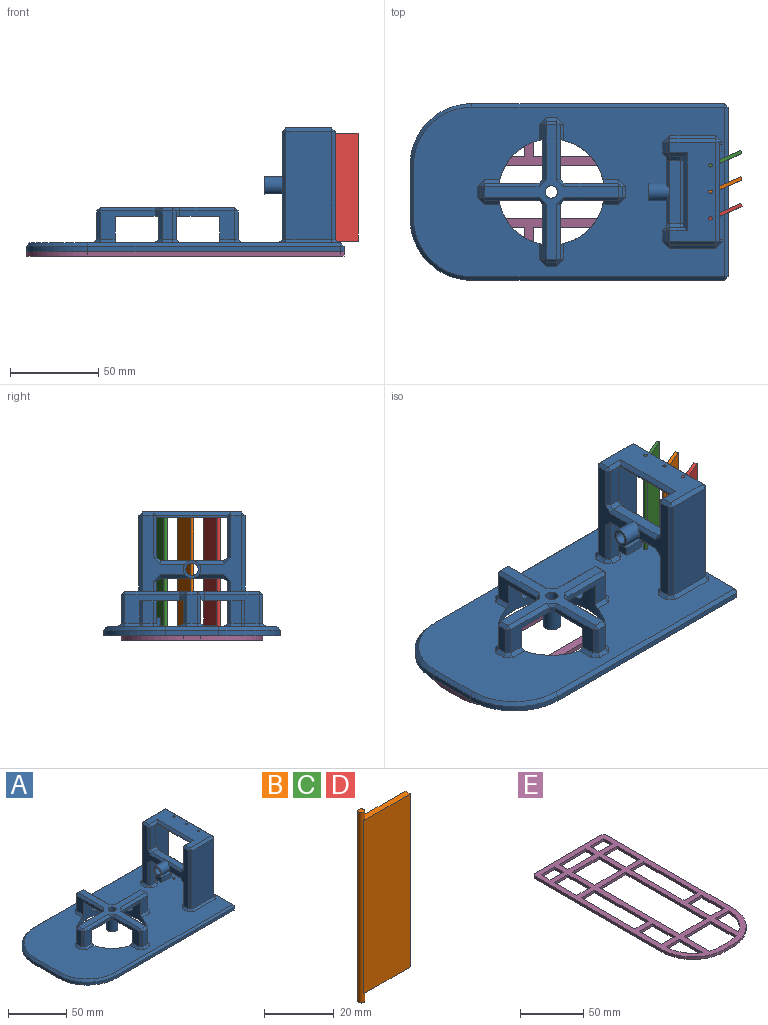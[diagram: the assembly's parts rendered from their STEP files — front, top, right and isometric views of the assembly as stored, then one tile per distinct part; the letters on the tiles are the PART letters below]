
ASSEMBLY  parts=5 mates=4
PART A: 192 faces, bbox 180x100x70 mm
  f0: plane 5x3mm, normal (-1,0,0), area 15mm2, adj f1,f2,f3,f189
  f1: plane 176x96mm, normal (0,0,1), area 12301.4mm2, adj f0,f3,f19,f26,f27,f28,f29,f48
  f2: plane 180x100mm, normal (0,0,-1), area 14548.4mm2, adj f0,f3,f20,f21,f22,f23,f24,f25
  f3: plane 67x22mm, normal (0,-1,0), area 1295mm2, adj f0,f1,f2,f4,f32,f34,f152,f181
  f4: plane 60x25.2mm, normal (1,0,0), area 430mm2, adj f3,f34,f117,f124,f125,f129,f175,f177
  f5: plane 61x24mm, normal (-1,0,0), area 485.9mm2, adj f118,f123,f126,f127,f130,f139,f148,f156
  f6: plane 61x24mm, normal (-1,0,0), area 485.9mm2, adj f118,f138,f143,f147,f155,f165,f166,f170
  f7: plane 60x25.2mm, normal (1,0,0), area 430mm2, adj f19,f34,f117,f120,f121,f125,f158,f168
  f8: plane 23.5x8mm, normal (0,-1,0), area 143mm2, adj f10,f34,f124,f137,f146,f147
  f9: plane 23.5x8mm, normal (0,1,0), area 143mm2, adj f10,f34,f120,f122,f123,f136
  f10: plane 40x1mm, normal (-1,0,0), area 40mm2, adj f8,f9,f34,f142
  f11: plane 76x76mm, normal (0,0,1), area 869.5mm2, adj f44,f64,f67,f72,f73,f76,f77,f84
  f12: plane 31x16mm, normal (0,-1,0), area 202.5mm2, adj f26,f45,f81,f91,f97,f98
  f13: plane 31x16mm, normal (0,1,0), area 202.5mm2, adj f26,f45,f70,f71,f83,f84
  f14: plane 10x10mm, normal (0,0,-1), area 40.1mm2, adj f44,f46
  f15: plane 31x16mm, normal (1,0,0), area 202.5mm2, adj f26,f45,f57,f62,f67,f68
  f16: plane 31x16mm, normal (-1,0,0), area 202.5mm2, adj f26,f45,f97,f102,f108,f109
  f17: plane 31x16mm, normal (1,0,0), area 202.5mm2, adj f26,f45,f96,f101,f106,f107
  f18: plane 31x16mm, normal (-1,0,0), area 202.5mm2, adj f26,f45,f58,f63,f71,f72
  f19: plane 62x22mm, normal (0,1,0), area 1240mm2, adj f1,f7,f32,f34,f132,f158
  f20: plane 30x3mm, normal (-1,0,0), area 90mm2, adj f2,f21,f25,f56
  f21: cylinder r=35mm len=35mm, axis (0,0,-1), area 164.9mm2, adj f2,f20,f22,f55
  f22: plane 143x3mm, normal (0,-1,0), area 429mm2, adj f2,f21,f49,f53
  f23: plane 96x3mm, normal (1,0,0), area 288mm2, adj f2,f47,f48,f49
  f24: plane 143x3mm, normal (0,1,0), area 429mm2, adj f2,f25,f47,f52
  f25: cylinder r=35mm len=35mm, axis (0,0,-1), area 164.9mm2, adj f2,f20,f24,f54
  f26: cylinder r=30mm len=60mm, axis (0,0,-1), area 1561.6mm2, adj f1,f2,f12,f13,f15,f16,f17,f18
  f27: cylinder r=1mm len=5mm, axis (0,0,-1), area 31.4mm2, adj f1,f2
  f28: cylinder r=1mm len=5mm, axis (0,0,-1), area 31.4mm2, adj f1,f2
  f29: cylinder r=1mm len=5mm, axis (0,0,-1), area 31.4mm2, adj f1,f2
  f30: plane 56x26mm, normal (0,0,1), area 1006.6mm2, adj f35,f36,f37,f127,f135,f136,f142,f145
  f31: plane 61x26mm, normal (0,1,0), area 1586mm2, adj f153,f154,f164,f165
  f32: plane 61x56mm, normal (1,0,0), area 176mm2, adj f3,f19,f34,f132,f134,f145,f152,f153
  f33: plane 61x26mm, normal (0,-1,0), area 1586mm2, adj f134,f135,f139,f140
  f34: plane 54x22mm, normal (0,0,-1), area 1074.6mm2, adj f3,f4,f7,f8,f9,f10,f19,f32
  f35: cylinder r=1mm len=3mm, axis (0,0,-1), area 18.8mm2, adj f30,f34
  f36: cylinder r=1mm len=3mm, axis (0,0,-1), area 18.8mm2, adj f30,f34
  f37: cylinder r=1mm len=3mm, axis (0,0,-1), area 18.8mm2, adj f30,f34
  f38: plane 31x16mm, normal (0,-1,0), area 202.5mm2, adj f26,f45,f80,f90,f95,f96
  f39: plane 31x16mm, normal (0,1,0), area 202.5mm2, adj f26,f45,f68,f69,f77,f78
  f40: plane 16x6mm, normal (-1,0,0), area 96mm2, adj f82,f83,f91,f92
  f41: plane 16x6mm, normal (0,-1,0), area 96mm2, adj f103,f106,f109,f112
  f42: plane 16x6mm, normal (1,0,0), area 96mm2, adj f78,f79,f89,f90
  f43: plane 16x6mm, normal (0,1,0), area 96mm2, adj f59,f62,f63,f64
  f44: cylinder r=3.5mm len=20mm, axis (0,0,-1), area 439.8mm2, adj f11,f14
  f45: plane 60x60mm, normal (0,0,-1), area 1023.9mm2, adj f12,f13,f15,f16,f17,f18,f26,f38
  f46: cylinder r=5mm len=15mm, axis (0,0,1), area 471.2mm2, adj f14,f45
  f47: plane 3x2mm, normal (0.71,0.71,0), area 8.5mm2, adj f2,f23,f24,f50
  f48: plane 96x2mm, normal (0.71,0,0.71), area 271.5mm2, adj f1,f23,f50,f51
  f49: plane 3x2mm, normal (0.71,-0.71,0), area 8.5mm2, adj f2,f22,f23,f51
  f50: plane 2x2mm, normal (0.58,0.58,0.58), area 3.5mm2, adj f47,f48,f52
  f51: plane 2x2mm, normal (0.58,-0.58,0.58), area 3.5mm2, adj f48,f49,f53
  f52: plane 143x2mm, normal (0,0.71,0.71), area 404.5mm2, adj f1,f24,f50,f54
  f53: plane 143x2mm, normal (0,-0.71,0.71), area 404.5mm2, adj f1,f22,f51,f55
  f54: cone r=33mm half-angle=45deg, axis (0,0,-1), area 151.1mm2, adj f1,f25,f52,f56
  f55: cone r=33mm half-angle=45deg, axis (0,0,-1), area 151.1mm2, adj f1,f21,f53,f56
  f56: plane 30x2mm, normal (-0.71,0,0.71), area 84.9mm2, adj f1,f20,f54,f55
  f57: plane 8.84x2.01mm, normal (0.71,0,0.71), area 24.4mm2, adj f1,f15,f26,f60
  f58: plane 8.84x2.01mm, normal (-0.71,0,0.71), area 24.4mm2, adj f1,f18,f26,f61
  f59: plane 6x2mm, normal (0,0.71,0.71), area 17mm2, adj f1,f43,f60,f61
  f60: plane 4x4mm, normal (0.58,0.58,0.58), area 10.4mm2, adj f1,f57,f59,f62
  f61: plane 4x4mm, normal (-0.58,0.58,0.58), area 10.4mm2, adj f1,f58,f59,f63
  f62: plane 16x2mm, normal (0.71,0.71,0), area 45.3mm2, adj f15,f43,f60,f65
  f63: plane 16x2mm, normal (-0.71,0.71,0), area 45.3mm2, adj f18,f43,f61,f66
  f64: plane 6x2mm, normal (0,0.71,0.71), area 17mm2, adj f11,f43,f65,f66
  f65: plane 2x2mm, normal (0.58,0.58,0.58), area 3.5mm2, adj f62,f64,f67
  f66: plane 2x2mm, normal (-0.58,0.58,0.58), area 3.5mm2, adj f63,f64,f72
  f67: plane 31x2mm, normal (0.71,0,0.71), area 87.7mm2, adj f11,f15,f65,f73
  f68: plane 3x2mm, normal (0.71,0.71,0), area 8.5mm2, adj f15,f39,f45,f73
  f69: plane 8.84x2.01mm, normal (0,0.71,0.71), area 24.4mm2, adj f1,f26,f39,f74
  f70: plane 8.84x2.01mm, normal (0,0.71,0.71), area 24.4mm2, adj f1,f13,f26,f75
  f71: plane 3x2mm, normal (-0.71,0.71,0), area 8.5mm2, adj f13,f18,f45,f76
  f72: plane 31x2mm, normal (-0.71,0,0.71), area 87.7mm2, adj f11,f18,f66,f76
  f73: plane 4x4mm, normal (0.58,0.58,0.58), area 10.4mm2, adj f11,f67,f68,f77
  f74: plane 4x4mm, normal (0.58,0.58,0.58), area 10.4mm2, adj f1,f69,f78,f79
  f75: plane 4x4mm, normal (-0.58,0.58,0.58), area 10.4mm2, adj f1,f70,f82,f83
  f76: plane 4x4mm, normal (-0.58,0.58,0.58), area 10.4mm2, adj f11,f71,f72,f84
  f77: plane 31x2mm, normal (0,0.71,0.71), area 87.7mm2, adj f11,f39,f73,f85
  f78: plane 16x2mm, normal (0.71,0.71,0), area 45.3mm2, adj f39,f42,f74,f85
  f79: plane 6x2mm, normal (0.71,0,0.71), area 17mm2, adj f1,f42,f74,f86
  f80: plane 8.84x2.01mm, normal (0,-0.71,0.71), area 24.4mm2, adj f1,f26,f38,f86
  f81: plane 8.84x2.01mm, normal (0,-0.71,0.71), area 24.4mm2, adj f1,f12,f26,f87
  f82: plane 6x2mm, normal (-0.71,0,0.71), area 17mm2, adj f1,f40,f75,f87
  f83: plane 16x2mm, normal (-0.71,0.71,0), area 45.3mm2, adj f13,f40,f75,f88
  f84: plane 31x2mm, normal (0,0.71,0.71), area 87.7mm2, adj f11,f13,f76,f88
  f85: plane 2x2mm, normal (0.58,0.58,0.58), area 3.5mm2, adj f77,f78,f89
  f86: plane 4x4mm, normal (0.58,-0.58,0.58), area 10.4mm2, adj f1,f79,f80,f90
  f87: plane 4x4mm, normal (-0.58,-0.58,0.58), area 10.4mm2, adj f1,f81,f82,f91
  f88: plane 2x2mm, normal (-0.58,0.58,0.58), area 3.5mm2, adj f83,f84,f92
  f89: plane 6x2mm, normal (0.71,0,0.71), area 17mm2, adj f11,f42,f85,f93
  f90: plane 16x2mm, normal (0.71,-0.71,0), area 45.3mm2, adj f38,f42,f86,f93
  f91: plane 16x2mm, normal (-0.71,-0.71,0), area 45.3mm2, adj f12,f40,f87,f94
  f92: plane 6x2mm, normal (-0.71,0,0.71), area 17mm2, adj f11,f40,f88,f94
  f93: plane 2x2mm, normal (0.58,-0.58,0.58), area 3.5mm2, adj f89,f90,f95
  f94: plane 2x2mm, normal (-0.58,-0.58,0.58), area 3.5mm2, adj f91,f92,f98
  f95: plane 31x2mm, normal (0,-0.71,0.71), area 87.7mm2, adj f11,f38,f93,f99
  f96: plane 3x2mm, normal (0.71,-0.71,0), area 8.5mm2, adj f17,f38,f45,f99
  f97: plane 3x2mm, normal (-0.71,-0.71,0), area 8.5mm2, adj f12,f16,f45,f100
  f98: plane 31x2mm, normal (0,-0.71,0.71), area 87.7mm2, adj f11,f12,f94,f100
  f99: plane 4x4mm, normal (0.58,-0.58,0.58), area 10.4mm2, adj f11,f95,f96,f101
  f100: plane 4x4mm, normal (-0.58,-0.58,0.58), area 10.4mm2, adj f11,f97,f98,f102
  f101: plane 31x2mm, normal (0.71,0,0.71), area 87.7mm2, adj f11,f17,f99,f104
  f102: plane 31x2mm, normal (-0.71,0,0.71), area 87.7mm2, adj f11,f16,f100,f105
  f103: plane 6x2mm, normal (0,-0.71,0.71), area 17mm2, adj f11,f41,f104,f105
  f104: plane 2x2mm, normal (0.58,-0.58,0.58), area 3.5mm2, adj f101,f103,f106
  f105: plane 2x2mm, normal (-0.58,-0.58,0.58), area 3.5mm2, adj f102,f103,f109
  f106: plane 16x2mm, normal (0.71,-0.71,0), area 45.3mm2, adj f17,f41,f104,f110
  f107: plane 8.84x2.01mm, normal (0.71,0,0.71), area 24.4mm2, adj f1,f17,f26,f110
  f108: plane 8.84x2.01mm, normal (-0.71,0,0.71), area 24.4mm2, adj f1,f16,f26,f111
  f109: plane 16x2mm, normal (-0.71,-0.71,0), area 45.3mm2, adj f16,f41,f105,f111
  f110: plane 4x4mm, normal (0.58,-0.58,0.58), area 10.4mm2, adj f1,f106,f107,f112
  f111: plane 4x4mm, normal (-0.58,-0.58,0.58), area 10.4mm2, adj f1,f108,f109,f112
  f112: plane 6x2mm, normal (0,-0.71,0.71), area 17mm2, adj f1,f41,f110,f111
  f113: plane 23.5x6mm, normal (0,-1,0), area 141mm2, adj f173,f174,f178,f179
  f114: plane 23.5x6mm, normal (0,1,0), area 141mm2, adj f156,f157,f167,f168
  f115: plane 36x6mm, normal (0,0,-1), area 216mm2, adj f161,f166,f167,f174,f175
  f116: plane 36x6mm, normal (0,0,1), area 216mm2, adj f122,f125,f130,f137,f138
  f117: cylinder r=3.5mm len=20mm, axis (1,0,0), area 437.3mm2, adj f4,f7,f119,f125,f175
  f118: cylinder r=5mm len=12mm, axis (1,0,0), area 338.5mm2, adj f5,f6,f119,f130,f138,f161,f166
  f119: plane 10x10mm, normal (-1,0,0), area 40.1mm2, adj f117,f118
  f120: plane 22.5x2mm, normal (0.71,0.71,0), area 63.6mm2, adj f7,f9,f34,f121
  f121: plane 4x4mm, normal (0.58,0.58,0.58), area 10.4mm2, adj f7,f120,f122,f125
  f122: plane 6x2mm, normal (0,0.71,0.71), area 17mm2, adj f9,f116,f121,f126
  f123: plane 23.5x2mm, normal (-0.71,0.71,0), area 66.5mm2, adj f5,f9,f126,f128
  f124: plane 22.5x2mm, normal (0.71,-0.71,0), area 63.6mm2, adj f4,f8,f34,f129
  f125: plane 36x2mm, normal (0.71,0,0.71), area 100.1mm2, adj f4,f7,f116,f117,f121,f129
  f126: plane 4x4mm, normal (-0.58,0.58,0.58), area 10.4mm2, adj f5,f122,f123,f130
  f127: plane 6x2mm, normal (-0.71,0,0.71), area 17mm2, adj f5,f30,f128,f131
  f128: plane 2x2mm, normal (-0.58,0.58,0.58), area 3.5mm2, adj f123,f127,f136
  f129: plane 4x4mm, normal (0.58,-0.58,0.58), area 10.4mm2, adj f4,f124,f125,f137
  f130: plane 18x2mm, normal (-0.71,0,0.71), area 43mm2, adj f5,f116,f118,f126
  f131: plane 2x2mm, normal (-0.58,-0.58,0.58), area 3.5mm2, adj f127,f135,f139
  f132: plane 2x2mm, normal (0.71,0,0.71), area 2.8mm2, adj f1,f19,f32,f133
  f133: plane 4x4mm, normal (0.58,-0.58,0.58), area 10.4mm2, adj f1,f132,f134,f140
  f134: plane 61x2mm, normal (0.71,-0.71,0), area 172.5mm2, adj f32,f33,f133,f141
  f135: plane 26x2mm, normal (0,-0.71,0.71), area 73.5mm2, adj f30,f33,f131,f141
  f136: plane 10x2mm, normal (0,0.71,0.71), area 25.5mm2, adj f9,f30,f128,f142
  f137: plane 6x2mm, normal (0,-0.71,0.71), area 17mm2, adj f8,f116,f129,f143
  f138: plane 18x2mm, normal (-0.71,0,0.71), area 43mm2, adj f6,f116,f118,f143
  f139: plane 61x2mm, normal (-0.71,-0.71,0), area 172.5mm2, adj f5,f33,f131,f144
  f140: plane 26x2mm, normal (0,-0.71,0.71), area 73.5mm2, adj f1,f33,f133,f144
  f141: plane 2x2mm, normal (0.58,-0.58,0.58), area 3.5mm2, adj f134,f135,f145
  f142: plane 44x2mm, normal (-0.71,0,0.71), area 118.8mm2, adj f10,f30,f136,f146
  f143: plane 4x4mm, normal (-0.58,-0.58,0.58), area 10.4mm2, adj f6,f137,f138,f147
  f144: plane 4x4mm, normal (-0.58,-0.58,0.58), area 10.4mm2, adj f1,f139,f140,f148
  f145: plane 56x2mm, normal (0.71,0,0.71), area 158.4mm2, adj f30,f32,f141,f149
  f146: plane 10x2mm, normal (0,-0.71,0.71), area 25.5mm2, adj f8,f30,f142,f150
  f147: plane 23.5x2mm, normal (-0.71,-0.71,0), area 66.5mm2, adj f6,f8,f143,f150
  f148: plane 6x2mm, normal (-0.71,0,0.71), area 17mm2, adj f1,f5,f144,f151
  f149: plane 2x2mm, normal (0.58,0.58,0.58), area 3.5mm2, adj f145,f153,f154
  f150: plane 2x2mm, normal (-0.58,-0.58,0.58), area 3.5mm2, adj f146,f147,f155
  f151: plane 4x4mm, normal (-0.58,0.58,0.58), area 10.4mm2, adj f1,f148,f156,f157
  f152: plane 2x2mm, normal (0.71,0,0.71), area 2.8mm2, adj f1,f3,f32,f159
  f153: plane 61x2mm, normal (0.71,0.71,0), area 172.5mm2, adj f31,f32,f149,f159
  f154: plane 26x2mm, normal (0,0.71,0.71), area 73.5mm2, adj f30,f31,f149,f160
  f155: plane 6x2mm, normal (-0.71,0,0.71), area 17mm2, adj f6,f30,f150,f160
  f156: plane 23.5x2mm, normal (-0.71,0.71,0), area 66.5mm2, adj f5,f114,f151,f162
  f157: plane 6x2mm, normal (0,0.71,0.71), area 17mm2, adj f1,f114,f151,f163
  f158: plane 5x2mm, normal (0.71,0,0.71), area 14.1mm2, adj f1,f7,f19,f163
  f159: plane 4x4mm, normal (0.58,0.58,0.58), area 10.4mm2, adj f1,f152,f153,f164
  f160: plane 2x2mm, normal (-0.58,0.58,0.58), area 3.5mm2, adj f154,f155,f165
  f161: plane 18x2mm, normal (-0.71,0,-0.71), area 43mm2, adj f5,f115,f118,f162
  f162: plane 4x4mm, normal (-0.58,0.58,-0.58), area 10.4mm2, adj f5,f156,f161,f167
  f163: plane 4x4mm, normal (0.58,0.58,0.58), area 10.4mm2, adj f1,f157,f158,f168
  f164: plane 26x2mm, normal (0,0.71,0.71), area 73.5mm2, adj f1,f31,f159,f169
  f165: plane 61x2mm, normal (-0.71,0.71,0), area 172.5mm2, adj f6,f31,f160,f169
  f166: plane 18x2mm, normal (-0.71,0,-0.71), area 43mm2, adj f6,f115,f118,f170
  f167: plane 6x2mm, normal (0,0.71,-0.71), area 17mm2, adj f114,f115,f162,f171
  f168: plane 23.5x2mm, normal (0.71,0.71,0), area 66.5mm2, adj f7,f114,f163,f171
  f169: plane 4x4mm, normal (-0.58,0.58,0.58), area 10.4mm2, adj f1,f164,f165,f172
  f170: plane 4x4mm, normal (-0.58,-0.58,-0.58), area 10.4mm2, adj f6,f166,f173,f174
  f171: plane 4x4mm, normal (0.58,0.58,-0.58), area 10.4mm2, adj f7,f167,f168,f175
  f172: plane 6x2mm, normal (-0.71,0,0.71), area 17mm2, adj f1,f6,f169,f176
  f173: plane 23.5x2mm, normal (-0.71,-0.71,0), area 66.5mm2, adj f6,f113,f170,f176
  f174: plane 6x2mm, normal (0,-0.71,-0.71), area 17mm2, adj f113,f115,f170,f177
  f175: plane 36x2mm, normal (0.71,0,-0.71), area 100.1mm2, adj f4,f7,f115,f117,f171,f177
  f176: plane 4x4mm, normal (-0.58,-0.58,0.58), area 10.4mm2, adj f1,f172,f173,f178
  f177: plane 4x4mm, normal (0.58,-0.58,-0.58), area 10.4mm2, adj f4,f174,f175,f179
  f178: plane 6x2mm, normal (0,-0.71,0.71), area 17mm2, adj f1,f113,f176,f180
  f179: plane 23.5x2mm, normal (0.71,-0.71,0), area 66.5mm2, adj f4,f113,f177,f180
  f180: plane 4x4mm, normal (0.58,-0.58,0.58), area 10.4mm2, adj f1,f178,f179,f181
  f181: plane 5x2mm, normal (0.71,0,0.71), area 14.1mm2, adj f1,f3,f4,f180
  f182: plane 10x6mm, normal (1,0,0), area 60mm2, adj f2,f3,f186,f187
  f183: plane 9x5mm, normal (-1,0,0), area 45mm2, adj f1,f3,f184,f187
  f184: plane 12x5mm, normal (0,-1,0), area 60mm2, adj f1,f183,f185,f187
  f185: plane 5x3mm, normal (1,0,0), area 15mm2, adj f1,f184,f186,f187
  f186: plane 14x10mm, normal (0,1,0), area 115mm2, adj f1,f2,f182,f185,f187,f188
  f187: plane 12x9mm, normal (0,0,1), area 54mm2, adj f3,f182,f183,f184,f185,f186
  f188: plane 5x2mm, normal (-1,0,0), area 10mm2, adj f1,f2,f186,f190
  f189: plane 5x1mm, normal (0,-1,0), area 5mm2, adj f0,f1,f2,f191
  f190: plane 5x1mm, normal (0,1,0), area 5mm2, adj f1,f2,f188,f191
  f191: plane 5x1mm, normal (-1,0,0), area 5mm2, adj f1,f2,f189,f190
PART B: 8 faces, bbox 20x2x67 mm
  f0: plane 2x2mm, normal (0,0,-1), area 3.1mm2, adj f7
  f1: plane 19x2mm, normal (0,0,-1), area 36.4mm2, adj f2,f5,f6,f7
  f2: plane 61x2mm, normal (1,0,0), area 122mm2, adj f1,f3,f5,f6
  f3: plane 19x2mm, normal (0,0,1), area 36.4mm2, adj f2,f5,f6,f7
  f4: plane 2x2mm, normal (0,0,1), area 3.1mm2, adj f7
  f5: plane 61x19mm, normal (0,-1,0), area 1159mm2, adj f1,f2,f3,f7
  f6: plane 61x19mm, normal (0,1,0), area 1159mm2, adj f1,f2,f3,f7
  f7: cylinder r=1mm len=67mm, axis (0,0,-1), area 229.3mm2, adj f0,f1,f3,f4,f5,f6
PART C: same geometry as B
PART D: same geometry as B
PART E: 66 faces, bbox 80x180x2.5 mm
  f0: plane 15x2.5mm, normal (0,1,0), area 37.5mm2, adj f1,f61,f62,f63
  f1: plane 25x2.5mm, normal (1,0,0), area 62.5mm2, adj f0,f2,f62,f63
  f2: plane 15x2.5mm, normal (0,-1,0), area 37.5mm2, adj f1,f61,f62,f63
  f3: plane 15x2.5mm, normal (0,1,0), area 37.5mm2, adj f4,f47,f62,f63
  f4: plane 60x2.5mm, normal (1,0,0), area 150mm2, adj f3,f5,f62,f63
  f5: plane 15x2.5mm, normal (0,-1,0), area 37.5mm2, adj f4,f47,f62,f63
  f6: plane 15x2.5mm, normal (0,1,0), area 37.5mm2, adj f7,f48,f62,f63
  f7: plane 25x2.5mm, normal (1,0,0), area 62.5mm2, adj f6,f8,f62,f63
  f8: plane 15x2.5mm, normal (0,-1,0), area 37.5mm2, adj f7,f48,f62,f63
  f9: plane 25.98x2.5mm, normal (-1,0,0), area 65mm2, adj f10,f49,f62,f63
  f10: cylinder r=30mm len=25.98mm, axis (0,0,-1), area 78.5mm2, adj f9,f49,f62,f63
  f11: plane 28.28x2.5mm, normal (-1,0,0), area 70.7mm2, adj f12,f50,f62,f63
  f12: cylinder r=30mm len=10mm, axis (0,0,-1), area 25.5mm2, adj f11,f13,f62,f63
  f13: plane 10x2.5mm, normal (0,1,0), area 25mm2, adj f12,f14,f62,f63
  f14: cylinder r=30mm len=10mm, axis (0,0,-1), area 25.5mm2, adj f13,f15,f62,f63
  f15: plane 28.28x2.5mm, normal (1,0,0), area 70.7mm2, adj f14,f50,f62,f63
  f16: plane 15x2.5mm, normal (0,-1,0), area 37.5mm2, adj f17,f51,f62,f63
  f17: cylinder r=30mm len=25.98mm, axis (0,0,-1), area 78.5mm2, adj f16,f51,f62,f63
  f18: plane 15x2.5mm, normal (0,-1,0), area 37.5mm2, adj f19,f52,f62,f63
  f19: plane 25x2.5mm, normal (-1,0,0), area 62.5mm2, adj f18,f20,f62,f63
  f20: plane 15x2.5mm, normal (0,1,0), area 37.5mm2, adj f19,f52,f62,f63
  f21: plane 15x2.5mm, normal (0,-1,0), area 37.5mm2, adj f22,f53,f62,f63
  f22: plane 60x2.5mm, normal (-1,0,0), area 150mm2, adj f21,f23,f62,f63
  f23: plane 15x2.5mm, normal (0,1,0), area 37.5mm2, adj f22,f53,f62,f63
  f24: plane 15x2.5mm, normal (0,-1,0), area 37.5mm2, adj f25,f54,f62,f63
  f25: plane 25x2.5mm, normal (-1,0,0), area 62.5mm2, adj f24,f26,f62,f63
  f26: plane 15x2.5mm, normal (0,1,0), area 37.5mm2, adj f25,f54,f62,f63
  f27: plane 10x2.5mm, normal (1,0,0), area 25mm2, adj f28,f55,f62,f63
  f28: plane 15x2.5mm, normal (0,-1,0), area 37.5mm2, adj f27,f29,f62,f63
  f29: plane 10x2.5mm, normal (-1,0,0), area 25mm2, adj f28,f55,f62,f63
  f30: plane 10x2.5mm, normal (1,0,0), area 25mm2, adj f31,f56,f62,f63
  f31: plane 30x2.5mm, normal (0,-1,0), area 75mm2, adj f30,f32,f62,f63
  f32: plane 10x2.5mm, normal (-1,0,0), area 25mm2, adj f31,f56,f62,f63
  f33: plane 76x2.5mm, normal (0,1,0), area 190mm2, adj f62,f63,f64,f65
  f34: plane 143x2.5mm, normal (-1,0,0), area 357.5mm2, adj f35,f62,f63,f64
  f35: cylinder r=35mm len=35mm, axis (0,0,-1), area 137.4mm2, adj f34,f36,f62,f63
  f36: plane 10x2.5mm, normal (0,-1,0), area 25mm2, adj f35,f37,f62,f63
  f37: cylinder r=35mm len=35mm, axis (0,0,-1), area 137.4mm2, adj f36,f57,f62,f63
  f38: plane 10x2.5mm, normal (1,0,0), area 25mm2, adj f39,f58,f62,f63
  f39: plane 15x2.5mm, normal (0,-1,0), area 37.5mm2, adj f38,f40,f62,f63
  f40: plane 10x2.5mm, normal (-1,0,0), area 25mm2, adj f39,f58,f62,f63
  f41: plane 30x2.5mm, normal (0,1,0), area 75mm2, adj f42,f59,f62,f63
  f42: plane 25x2.5mm, normal (1,0,0), area 62.5mm2, adj f41,f43,f62,f63
  f43: plane 30x2.5mm, normal (0,-1,0), area 75mm2, adj f42,f59,f62,f63
  f44: plane 90x2.5mm, normal (1,0,0), area 225mm2, adj f45,f60,f62,f63
  f45: plane 30x2.5mm, normal (0,-1,0), area 75mm2, adj f44,f46,f62,f63
  f46: plane 90x2.5mm, normal (-1,0,0), area 225mm2, adj f45,f60,f62,f63
  f47: plane 60x2.5mm, normal (-1,0,0), area 150mm2, adj f3,f5,f62,f63
  f48: plane 25x2.5mm, normal (-1,0,0), area 62.5mm2, adj f6,f8,f62,f63
  f49: plane 15x2.5mm, normal (0,-1,0), area 37.5mm2, adj f9,f10,f62,f63
  f50: plane 30x2.5mm, normal (0,-1,0), area 75mm2, adj f11,f15,f62,f63
  f51: plane 25.98x2.5mm, normal (1,0,0), area 65mm2, adj f16,f17,f62,f63
  f52: plane 25x2.5mm, normal (1,0,0), area 62.5mm2, adj f18,f20,f62,f63
  f53: plane 60x2.5mm, normal (1,0,0), area 150mm2, adj f21,f23,f62,f63
  f54: plane 25x2.5mm, normal (1,0,0), area 62.5mm2, adj f24,f26,f62,f63
  f55: plane 15x2.5mm, normal (0,1,0), area 37.5mm2, adj f27,f29,f62,f63
  f56: plane 30x2.5mm, normal (0,1,0), area 75mm2, adj f30,f32,f62,f63
  f57: plane 143x2.5mm, normal (1,0,0), area 357.5mm2, adj f37,f62,f63,f65
  f58: plane 15x2.5mm, normal (0,1,0), area 37.5mm2, adj f38,f40,f62,f63
  f59: plane 25x2.5mm, normal (-1,0,0), area 62.5mm2, adj f41,f43,f62,f63
  f60: plane 30x2.5mm, normal (0,1,0), area 75mm2, adj f44,f46,f62,f63
  f61: plane 25x2.5mm, normal (-1,0,0), area 62.5mm2, adj f0,f2,f62,f63
  f62: plane 180x80mm, normal (0,0,1), area 5078.8mm2, adj f0,f1,f2,f3,f4,f5,f6,f7
  f63: plane 180x80mm, normal (0,0,-1), area 5078.8mm2, adj f0,f1,f2,f3,f4,f5,f6,f7
  f64: plane 2.5x2mm, normal (-0.71,0.71,0), area 7.1mm2, adj f33,f34,f62,f63
  f65: plane 2.5x2mm, normal (0.71,0.71,0), area 7.1mm2, adj f33,f57,f62,f63
PLACE A t=(-20.87,43,-2.86)mm fixed
PLACE B rot(axis=(0,0,1),23.3deg) t=(136.17,45.1,40.21)mm
PLACE C rot(axis=(0,0,1),23.3deg) t=(136.17,60.1,40.21)mm
PLACE D rot(axis=(0,0,1),23.3deg) t=(136.17,30.1,40.21)mm
PLACE E rot(axis=(0,0,-1),90deg) t=(8.86,9.81,-5.36)mm
MATE revolute C.f7 <-> A.f27  axis (0,0,1) through (68.91,30.02,64.14)mm
MATE revolute B.f7 <-> A.f28  axis (0,0,1) through (68.91,15.02,64.14)mm
MATE revolute A.f29 <-> D.f7  axis (0,0,-1) through (68.91,0.02,64.14)mm
MATE slider A.f2 <-> E.f62  axis (0,0,-1) through (78.91,15.02,-2.86)mm
